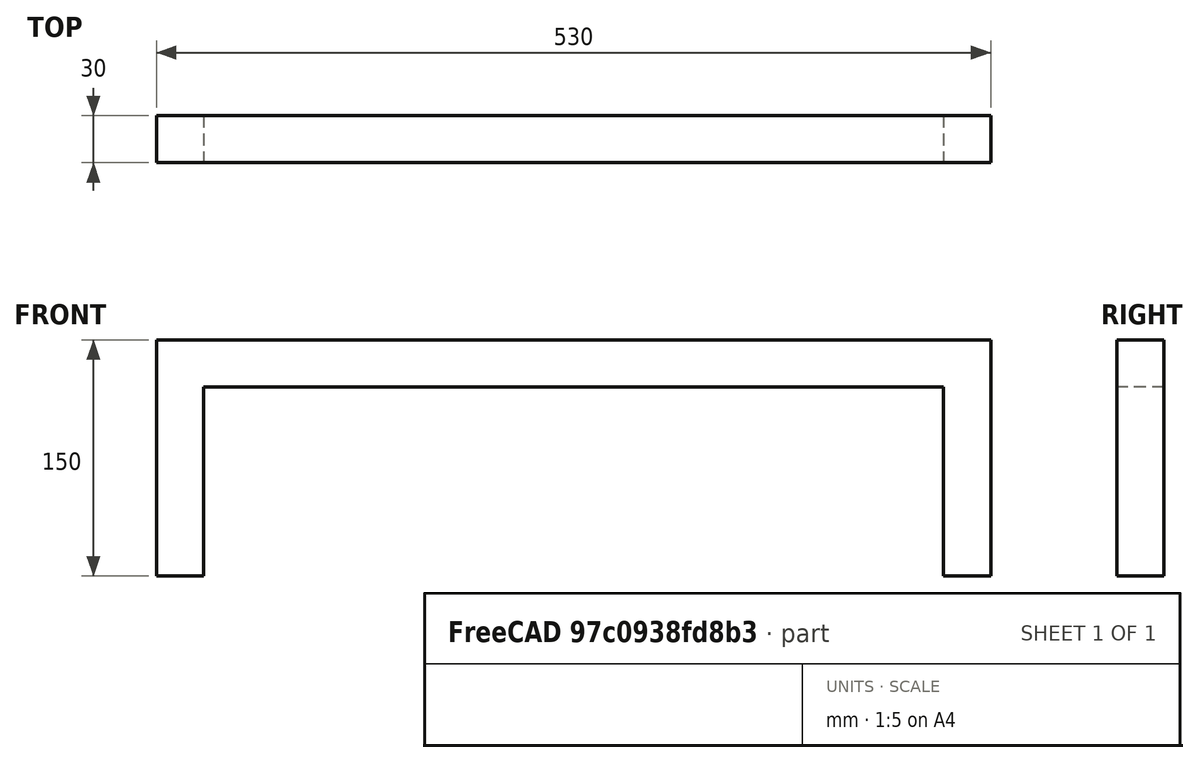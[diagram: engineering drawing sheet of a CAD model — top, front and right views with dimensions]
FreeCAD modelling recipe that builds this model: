
FCSTD DOCUMENT  (FreeCAD 0.16R6348 (Git))
Label: ChasisFrontal1
License: All rights reserved
LicenseURL: http://es.wikipedia.org/wiki/Todos_los_derechos_reservados
objects: Sketcher::SketchObject×1, PartDesign::Pad×1, Part::Feature×1
note: 4 computed .brp shape members not serialized (recipe doc carries the construction recipe); baked Part::Feature solids carry a one-line shape summary decoded from their .brp

FEATURE [Sketcher::SketchObject] Sketch
  Placement = pos=(0,0,0) rot=(-1,0,0;4.71239rad)
  sketch-geometry (8):
    g0: LineSegment StartX=0 StartY=0 StartZ=0 EndX=0 EndY=150 EndZ=0
    g1: LineSegment StartX=0 StartY=150 StartZ=0 EndX=530 EndY=150 EndZ=0
    g2: LineSegment StartX=530 StartY=150 StartZ=0 EndX=530 EndY=0 EndZ=0
    g3: LineSegment StartX=530 StartY=0 StartZ=0 EndX=500 EndY=0 EndZ=0
    g4: LineSegment StartX=500 StartY=0 StartZ=0 EndX=500 EndY=120 EndZ=0
    g5: LineSegment StartX=500 StartY=120 StartZ=0 EndX=30 EndY=120 EndZ=0
    g6: LineSegment StartX=30 StartY=120 StartZ=0 EndX=30 EndY=0 EndZ=0
    g7: LineSegment StartX=30 StartY=0 StartZ=0 EndX=0 EndY=0 EndZ=0
  constraints (25):
    c: PointOnObject(g0,g-2)
    c: Vertical(g0)
    c: Coincident(g0,g1)
    c: Horizontal(g1)
    c: Coincident(g1,g2)
    c: Vertical(g2)
    c: Coincident(g2,g3)
    c: Horizontal(g3)
    c: Coincident(g3,g4)
    c: Vertical(g4)
    c: Coincident(g4,g5)
    c: Horizontal(g5)
    c: Coincident(g5,g6)
    c: Vertical(g6)
    c: Coincident(g6,g7)
    c: Coincident(g7,g-1)
    c: Horizontal(g7)
    c: DistanceY(g0) = 150
    c: Coincident(g0,g-1)
    c: DistanceX(g-1,g6) = 30
    c: DistanceY(g0,g5) = -30
    c: DistanceX(g0,g1) = 530
    c: Equal(g0,g2)
    c: Equal(g6,g4)
    c: Equal(g7,g3)
FEATURE [PartDesign::Pad] Pad
  Length = 30
  Length2 = 100
  Placement = pos=(0,0,0) rot=(-1,0,0;4.71239rad)
  Sketch = -> Sketch
  Type = 0
FEATURE [Part::Feature] Pad001
  Placement = pos=(0,0,0) rot=(1,0,0;1.5708rad)
  shape: bbox 530 x 30 x 150 mm, 10 faces (baked)
